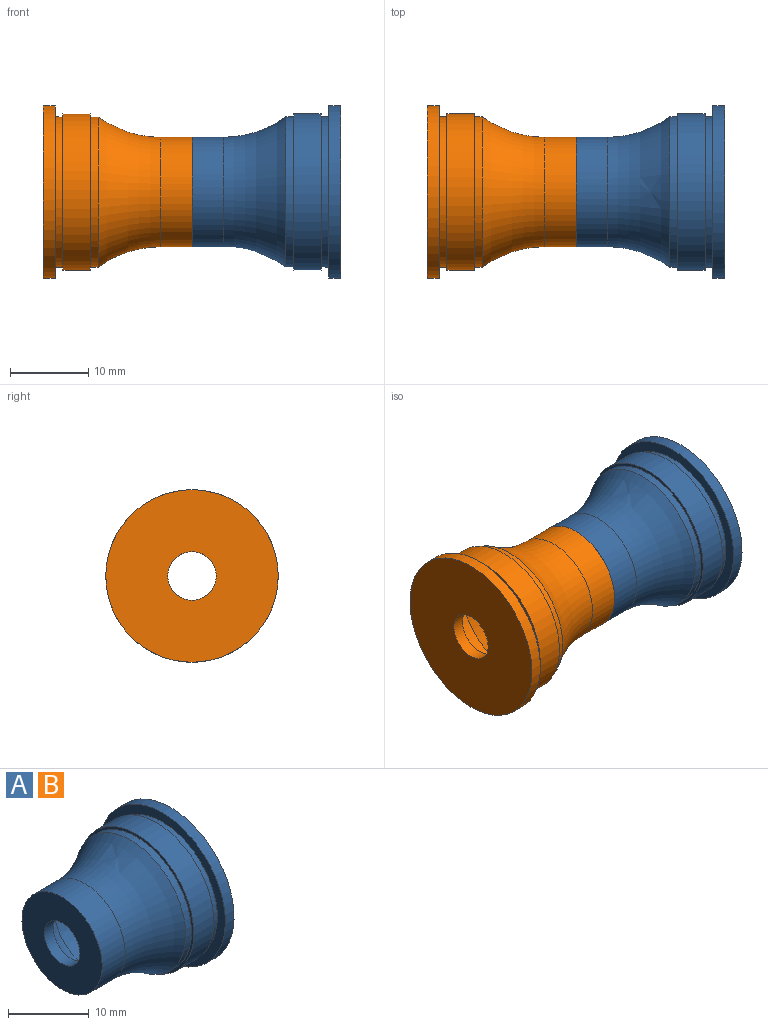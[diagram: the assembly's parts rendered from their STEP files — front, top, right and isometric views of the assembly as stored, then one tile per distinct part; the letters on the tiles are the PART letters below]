
ASSEMBLY  parts=2 mates=1
PART A: 20 faces, bbox 19x23.7x23.7 mm
  f0: plane 14x14mm, normal (-1,0,0), area 123.7mm2, adj f1,f19
  f1: cylinder r=3.1mm len=6.2mm, axis (-1,0,0), area 30.4mm2, adj f0,f2
  f2: plane 7.33x7.33mm, normal (1,0,0), area 12mm2, adj f1,f3
  f3: torus R=1.59mm, axis (-1,0,0), area 119mm2, adj f2,f4
  f4: cone r=5.89mm half-angle=12.5deg, axis (1,0,0), area 89.7mm2, adj f3,f5
  f5: torus R=22.46mm, axis (-1,0,0), area 270.9mm2, adj f4,f6
  f6: cylinder r=8.64mm len=17.29mm, axis (-1,0,0), area 281mm2, adj f5,f7
  f7: cone r=8.64mm half-angle=83.3deg, axis (-1,0,0), area 124.2mm2, adj f6,f8
  f8: cone r=5.96mm half-angle=86.2deg, axis (1,0,0), area 81.4mm2, adj f7,f9
  f9: cylinder r=3.1mm len=6.2mm, axis (-1,0,0), area 30.4mm2, adj f8,f10
  f10: plane 22.06x22.06mm, normal (1,0,0), area 351.9mm2, adj f9,f11
  f11: cylinder r=11.03mm len=22.06mm, axis (-1,0,0), area 105.8mm2, adj f10,f12
  f12: cone r=9.62mm half-angle=88.9deg, axis (-1,0,0), area 91.4mm2, adj f11,f13
  f13: cone r=9.6mm half-angle=1.1deg, axis (1,0,0), area 60.4mm2, adj f12,f14
  f14: plane 20x20mm, normal (1,0,0), area 24.6mm2, adj f13,f15
  f15: cylinder r=10mm len=20mm, axis (-1,0,0), area 219.9mm2, adj f14,f16
  f16: plane 20x20mm, normal (-1,0,0), area 24.6mm2, adj f15,f17
  f17: cylinder r=9.6mm len=19.2mm, axis (-1,0,0), area 60.3mm2, adj f16,f18
  f18: torus R=20.57mm, axis (-1,0,0), area 422.7mm2, adj f17,f19
  f19: cylinder r=7mm len=14mm, axis (-1,0,0), area 176.5mm2, adj f0,f18
PART B: same geometry as A
PLACE A t=(7.33,8.71,-1.51)mm
PLACE B rot(axis=(0,1,0),180deg) t=(7.33,8.71,-1.51)mm
MATE revolute B.f1 <-> A.f1  axis (1,0,0) through (7.33,8.71,-1.51)mm
